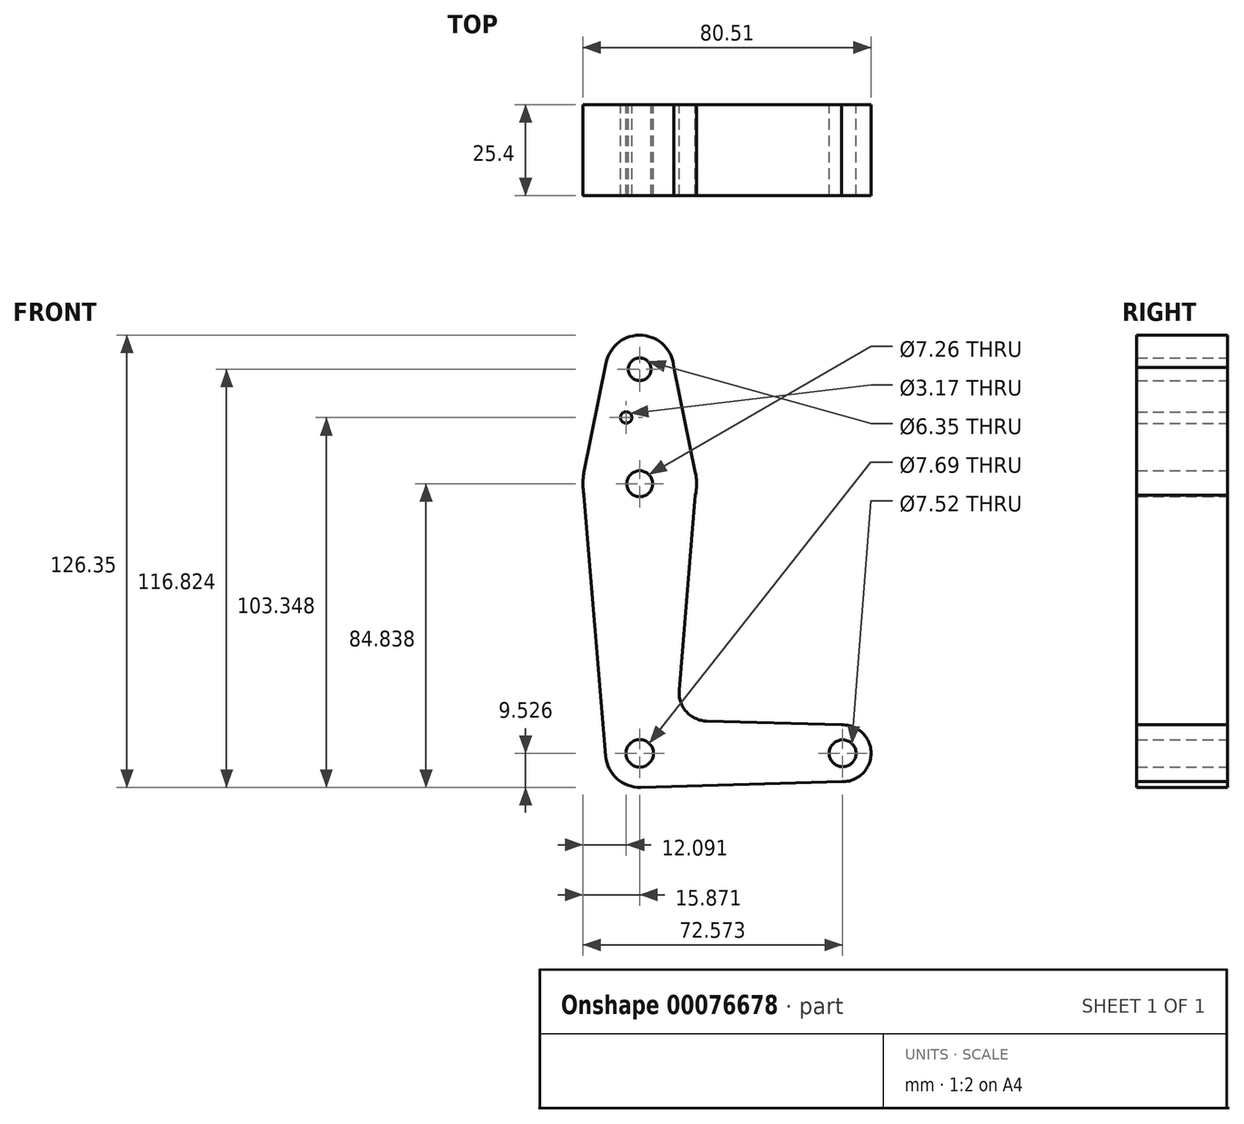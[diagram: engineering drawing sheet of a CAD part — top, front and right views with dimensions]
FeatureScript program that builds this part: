
annotation { "Feature Type Name" : "Feature", "Feature Type Description" : "" }
export const myFeature = defineFeature(function(context is Context, id is Id, definition is map)
    precondition{}
    {
        {
            var Q0;
            Q0=qCreatedBy(makeId("Front.planeOp"),FACE);
            var sketch = newSketch(context, id + "F0", { "sketchPlane" : qUnion([Q0])});
            skLineSegment(sketch, "E0", {"start": v(-33.97, 59.06) * mm, "end": v(-33.97, -48.23) * mm, "construction": true});
            skLineSegment(sketch, "E1", {"start": v(-33.97, -48.23) * mm, "end": v(22.73, -48.23) * mm, "construction": true});
            skCircle(sketch, "E2", {"center": v(-33.97, 59.06) * mm, "radius": 9.53 * mm});
            skCircle(sketch, "E3", {"center": v(-33.97, 27.08) * mm, "radius": 15.88 * mm});
            skCircle(sketch, "E4", {"center": v(-33.97, -48.23) * mm, "radius": 9.53 * mm});
            skCircle(sketch, "E5", {"center": v(22.73, -48.23) * mm, "radius": 7.94 * mm});
            skLineSegment(sketch, "E6", {"start": v(-43.3, 60.95) * mm, "end": v(-49.53, 30.23) * mm});
            skLineSegment(sketch, "E7", {"start": v(-49.53, 30.23) * mm, "end": v(-49.53, 23.93) * mm});
            skLineSegment(sketch, "E8", {"start": v(-49.53, 23.93) * mm, "end": v(-43.46, -49.02) * mm});
            skLineSegment(sketch, "E9", {"start": v(-25.04, 62.39) * mm, "end": v(-18.42, 30.29) * mm});
            skLineSegment(sketch, "E10", {"start": v(-18.42, 30.29) * mm, "end": v(-18.42, 23.87) * mm});
            skLineSegment(sketch, "E11", {"start": v(-18.42, 23.87) * mm, "end": v(-22.95, -30.63) * mm});
            skLineSegment(sketch, "E12", {"start": v(22.45, -40.3) * mm, "end": v(-15.25, -39.23) * mm});
            skLineSegment(sketch, "E13", {"start": v(23.38, -56.15) * mm, "end": v(-33.7, -57.76) * mm});
            skCircle(sketch, "E14", {"center": v(-33.97, 59.06) * mm, "radius": 3.18 * mm});
            skCircle(sketch, "E15", {"center": v(-33.97, 27.08) * mm, "radius": 3.63 * mm});
            skCircle(sketch, "E16", {"center": v(-33.97, -48.23) * mm, "radius": 3.85 * mm});
            skCircle(sketch, "E17", {"center": v(22.73, -48.23) * mm, "radius": 3.76 * mm});
            skCircle(sketch, "E18", {"center": v(-37.75, 45.59) * mm, "radius": 1.59 * mm});
            skPoint(sketch, "E18.centerSnap0", {"position": v(-46.42, 45.59) * mm});
            skArc(sketch, "E19.filletArc", {"start": v(-22.95, -30.63) * mm, "mid": v(-20.95, -36.59) * mm, "end": v(-15.25, -39.23) * mm});
            skSolve(sketch);
        }
        {
            var Q0;
            Q0 = qSketchRegion(id + "F0", true);
            extrude(context, id + "F1", {"entities" : qUnion([Q0]), "depth" : 25.4 * mm});
        }
    });
